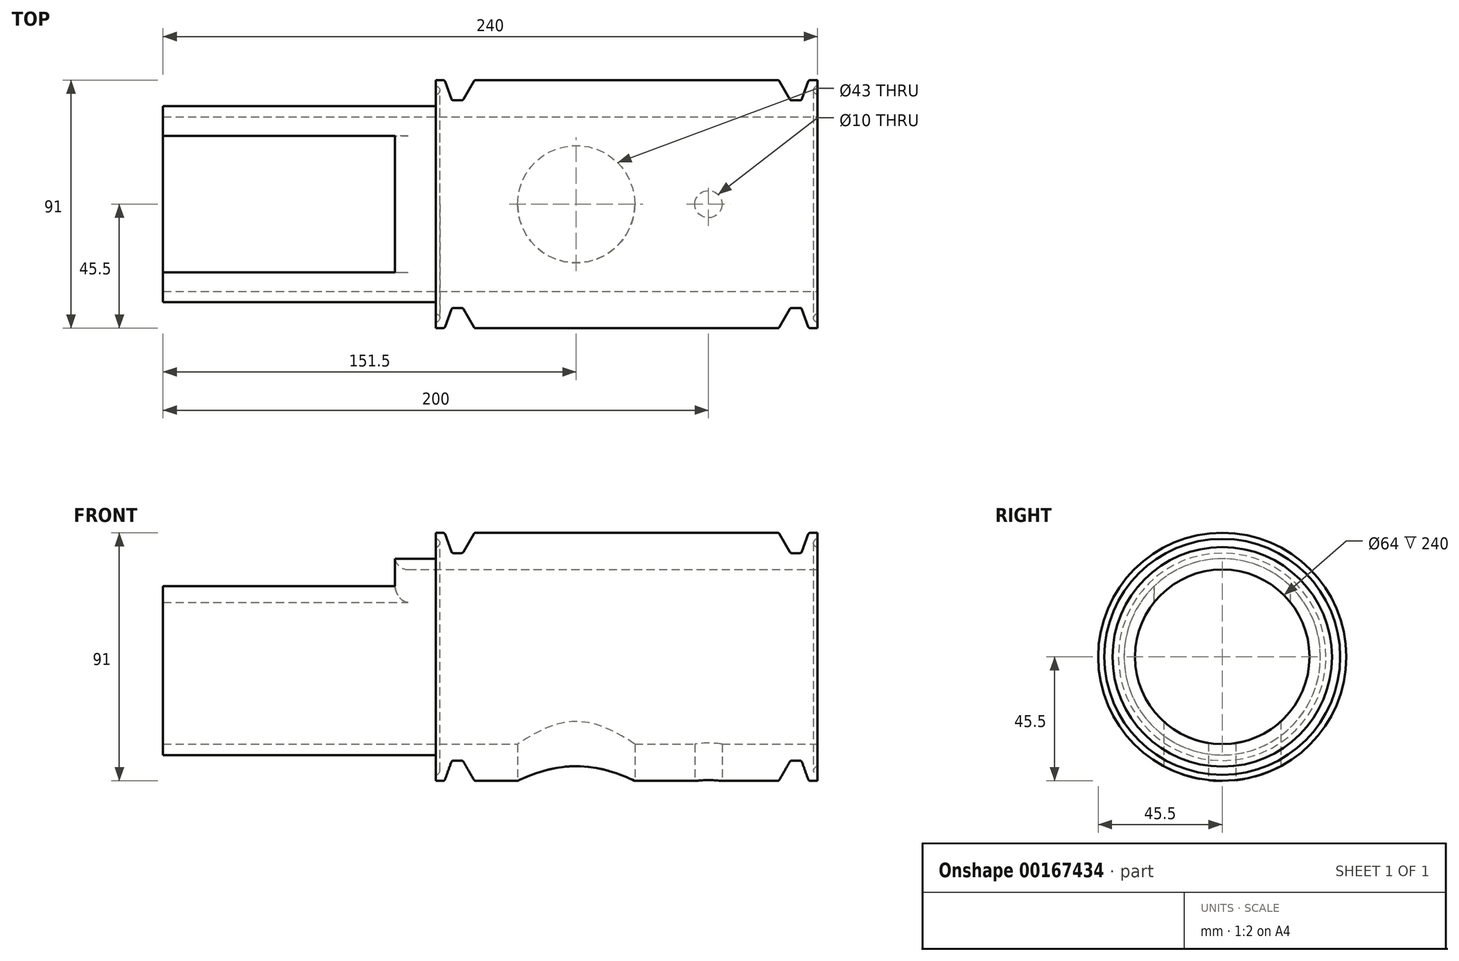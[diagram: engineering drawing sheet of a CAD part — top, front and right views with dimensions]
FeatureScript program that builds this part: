
annotation { "Feature Type Name" : "Feature", "Feature Type Description" : "" }
export const myFeature = defineFeature(function(context is Context, id is Id, definition is map)
    precondition{}
    {
        {
            var Q0;
            Q0=qCreatedBy(makeId("Front.planeOp"),FACE);
            var sketch = newSketch(context, id + "F0", { "sketchPlane" : qUnion([Q0])});
            skLineSegment(sketch, "E0", {"start": v(0, 0) * mm, "end": v(-76.74, 0) * mm, "construction": true});
            skLineSegment(sketch, "E1", {"start": v(-240, 32) * mm, "end": v(0, 32) * mm});
            skLineSegment(sketch, "E2", {"start": v(0, 32) * mm, "end": v(0, 40.25) * mm});
            skLineSegment(sketch, "E3", {"start": v(0, 45.5) * mm, "end": v(-2.64, 45.5) * mm});
            skLineSegment(sketch, "E4", {"start": v(-3.4, 44.97) * mm, "end": v(-5.72, 38.58) * mm});
            skLineSegment(sketch, "E5", {"start": v(-6.47, 38.05) * mm, "end": v(-9.45, 38.05) * mm});
            skLineSegment(sketch, "E6", {"start": v(-10.14, 38.45) * mm, "end": v(-13.98, 45.1) * mm});
            skLineSegment(sketch, "E7", {"start": v(-14.67, 45.5) * mm, "end": v(-125.33, 45.5) * mm});
            skLineSegment(sketch, "E8", {"start": v(-126.02, 45.1) * mm, "end": v(-129.86, 38.45) * mm});
            skLineSegment(sketch, "E9", {"start": v(-130.55, 38.05) * mm, "end": v(-133.53, 38.05) * mm});
            skLineSegment(sketch, "E10", {"start": v(-134.28, 38.58) * mm, "end": v(-136.6, 44.97) * mm});
            skLineSegment(sketch, "E11", {"start": v(-137.36, 45.5) * mm, "end": v(-140, 45.5) * mm});
            skLineSegment(sketch, "E12", {"start": v(-140, 45.5) * mm, "end": v(-140, 43.25) * mm});
            skLineSegment(sketch, "E13", {"start": v(-140, 36) * mm, "end": v(-240, 36) * mm});
            skLineSegment(sketch, "E14", {"start": v(-240, 36) * mm, "end": v(-240, 32) * mm});
            skArc(sketch, "E15", {"start": v(0, 43.25) * mm, "mid": v(-1.5, 41.75) * mm, "end": v(0, 40.25) * mm});
            skArc(sketch, "E16", {"start": v(-140, 40.25) * mm, "mid": v(-138.5, 41.75) * mm, "end": v(-140, 43.25) * mm});
            skLineSegment(sketch, "E17.trimOffspring", {"start": v(0, 43.25) * mm, "end": v(0, 45.5) * mm});
            skLineSegment(sketch, "E18.trimOffspring", {"start": v(-140, 40.25) * mm, "end": v(-140, 36) * mm});
            skPoint(sketch, "E19.visualSharp", {"position": v(-3.2, 45.5) * mm});
            skArc(sketch, "E19.filletArc", {"start": v(-2.64, 45.5) * mm, "mid": v(-3.1, 45.36) * mm, "end": v(-3.4, 44.97) * mm});
            skPoint(sketch, "E20.visualSharp", {"position": v(-5.91, 38.05) * mm});
            skArc(sketch, "E20.filletArc", {"start": v(-6.47, 38.05) * mm, "mid": v(-6.01, 38.2) * mm, "end": v(-5.72, 38.58) * mm});
            skPoint(sketch, "E21.visualSharp", {"position": v(-9.91, 38.05) * mm});
            skArc(sketch, "E21.filletArc", {"start": v(-10.14, 38.45) * mm, "mid": v(-9.85, 38.16) * mm, "end": v(-9.45, 38.05) * mm});
            skPoint(sketch, "E22.visualSharp", {"position": v(-14.21, 45.5) * mm});
            skArc(sketch, "E22.filletArc", {"start": v(-13.98, 45.1) * mm, "mid": v(-14.27, 45.4) * mm, "end": v(-14.67, 45.5) * mm});
            skPoint(sketch, "E23.visualSharp", {"position": v(-125.79, 45.5) * mm});
            skArc(sketch, "E23.filletArc", {"start": v(-125.33, 45.5) * mm, "mid": v(-125.73, 45.4) * mm, "end": v(-126.02, 45.1) * mm});
            skPoint(sketch, "E24.visualSharp", {"position": v(-130.09, 38.05) * mm});
            skArc(sketch, "E24.filletArc", {"start": v(-130.55, 38.05) * mm, "mid": v(-130.15, 38.16) * mm, "end": v(-129.86, 38.45) * mm});
            skPoint(sketch, "E25.visualSharp", {"position": v(-134.09, 38.05) * mm});
            skArc(sketch, "E25.filletArc", {"start": v(-134.28, 38.58) * mm, "mid": v(-133.99, 38.2) * mm, "end": v(-133.53, 38.05) * mm});
            skPoint(sketch, "E26.visualSharp", {"position": v(-136.8, 45.5) * mm});
            skArc(sketch, "E26.filletArc", {"start": v(-136.6, 44.97) * mm, "mid": v(-136.9, 45.36) * mm, "end": v(-137.36, 45.5) * mm});
            skSolve(sketch);
        }
        {
            var Q0;
            Q0=qSketchRegion(id+"F0",true);
            var Q1;
            Q1=sQuery(id+"F0.wireOp",EDGE,"E0");
            revolve(context, id + "F1", {"entities" : qUnion([Q0]), "axis" : qUnion([Q1]), "revolveType" : RevolveType.FULL});
        }
        {
            var Q0;
            Q0=qCreatedBy(makeId("Top.planeOp"),FACE);
            cPlane(context, id + "F2", {"entities" : qUnion([Q0]), "cplaneType" : CPlaneType.OFFSET, "offset" : 45.5 * mm, "oppositeDirection" : true, "width" : 150 * mm, "height" : 150 * mm});
        }
        {
            var Q0;
            Q0=qCreatedBy(id+"F2.planeOp",FACE);
            var sketch = newSketch(context, id + "F3", { "sketchPlane" : qUnion([Q0])});
            skCircle(sketch, "E27", {"center": v(-88.5, 0) * mm, "radius": 21.5 * mm});
            skCircle(sketch, "E28", {"center": v(-88.5, 0) * mm, "radius": 25.4 * mm, "construction": true});
            skSolve(sketch);
        }
        {
            var Q0;
            Q0=qSketchRegion(id+"F3",true);
            extrude(context, id + "F4", {"entities" : qUnion([Q0]), "operationType" : NewBodyOperationType.REMOVE, "depth" : 25 * mm});
        }
        {
            var Q0;
            Q0=qCreatedBy(makeId("Top.planeOp"),FACE);
            cPlane(context, id + "F5", {"entities" : qUnion([Q0]), "cplaneType" : CPlaneType.OFFSET, "offset" : 45.5 * mm, "width" : 150 * mm, "height" : 150 * mm});
        }
        {
            var Q0;
            Q0=qCreatedBy(id+"F5.planeOp",FACE);
            var sketch = newSketch(context, id + "F6", { "sketchPlane" : qUnion([Q0])});
            skLineSegment(sketch, "E29", {"start": v(0, 0) * mm, "end": v(-198.27, 0) * mm, "construction": true});
            skLineSegment(sketch, "E30.1", {"start": v(-240, 36) * mm, "end": v(-240, -36) * mm, "construction": true});
            skLineSegment(sketch, "E31.bottom", {"start": v(-240, 25) * mm, "end": v(-155, 25) * mm});
            skLineSegment(sketch, "E31.top", {"start": v(-240, -25) * mm, "end": v(-155, -25) * mm});
            skLineSegment(sketch, "E31.left", {"start": v(-240, 25) * mm, "end": v(-240, -25) * mm});
            skLineSegment(sketch, "E31.right", {"start": v(-155, 25) * mm, "end": v(-155, -25) * mm});
            skPoint(sketch, "E31.middle", {"position": v(-197.5, 0) * mm});
            skSolve(sketch);
        }
        {
            var Q0;
            Q0=qSketchRegion(id+"F6",true);
            extrude(context, id + "F7", {"entities" : qUnion([Q0]), "operationType" : NewBodyOperationType.REMOVE, "oppositeDirection" : true, "depth" : 30 * mm});
        }
        {
            var Q0;
            Q0=makeQuery(id+"F7.boolean.opBoolean","INTERSECT",EDGE,{"derivedFrom":[makeQuery(id+"F1.opRevolve","SWEPT_FACE",FACE,{"disambiguationData":[OSD([sQuery(id+"F0.wireOp",EDGE,"E1")])]}),makeQuery(id+"F7.opExtrude","SWEPT_FACE",FACE,{"disambiguationData":[OSD([sQuery(id+"F6.wireOp",EDGE,"E31.right")])]})]});
            fillet(context, id + "F8", {"entities" : qUnion([Q0]), "radius" : 5 * mm, "tangentPropagation" : true, "allowEdgeOverflow" : false});
        }
        {
            var Q0;
            Q0=qCreatedBy(id+"F2.planeOp",FACE);
            var sketch = newSketch(context, id + "F9", { "sketchPlane" : qUnion([Q0])});
            skCircle(sketch, "E32", {"center": v(-40, 0) * mm, "radius": 5 * mm});
            skSolve(sketch);
        }
        {
            var Q0;
            Q0 = qSketchRegion(id + "F9", true);
            extrude(context, id + "F10", {"entities" : qUnion([Q0]), "operationType" : NewBodyOperationType.REMOVE, "depth" : 50 * mm});
        }
    });
